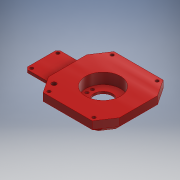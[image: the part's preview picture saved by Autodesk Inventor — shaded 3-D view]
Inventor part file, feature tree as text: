
AUTODESK INVENTOR PART (.ipt)
format: ipt  version: 2018 (Build 220112000, 112)  size: 877,568 bytes
history: native  units: mm
features: sketch x21, extrude x20, mirror x5, projected_geometry x4, chamfer x2, other x2, pattern_circular x2, fillet x1
ambient origin geometry x8: Origin, YZ Plane, XZ Plane, XY Plane, X Axis, Y Axis, Z Axis, Center Point
bodies: Body1 (feature_tree)
feature tree (57):
  extrude  "押し出し2"  Depth=12.0mm TaperAngle=0.0deg
  extrude  "押し出し3"  Depth=17.0mm
  extrude  "押し出し4"  Depth=10.0mm TaperAngle=0.0deg
  extrude  "押し出し5"  Depth=36.5mm
  extrude  "押し出し6"  Depth=6.0mm TaperAngle=0.0deg
  chamfer  "面取り1"  Distance=25.0mm
  extrude  "押し出し7"  Depth=3.0mm
  extrude  "押し出し8"  Depth=3.0mm
  mirror  "ミラー1"
  other  "作業平面1"
  extrude  "押し出し9"  Depth=2.5mm
  extrude  "押し出し10"  Depth=5.0mm TaperAngle=0.0deg
  pattern_circular  "円形状パターン1"  [2 undecoded]
  sketch  "スケッチ12"
  extrude  "押し出し12"  Depth=2.0mm
  pattern_circular  "円形状パターン2"  [2 undecoded]
  extrude  "押し出し11"  Depth=2.0mm
  extrude  "押し出し13"  Depth=4.0mm TaperAngle=0.0deg
  extrude  "押し出し14"  Depth=2.0mm TaperAngle=45.0deg
  mirror  "ミラー3"
  extrude  "押し出し15"  Depth=2.0mm
  extrude  "押し出し16"  Depth=5.0mm
  fillet  "フィレット1"  Radius=7.0mm
  mirror  "ミラー4"
  chamfer  "面取り3"  Angle=45.0deg  [1 undecoded]
  extrude  "押し出し17"  Depth=3.0mm
  mirror  "ミラー5"
  mirror  "ミラー6"
  other  "エンボス1"
  extrude  "押し出し20"  Depth=3.0mm
  extrude  "押し出し19"  Depth=60.0mm
  extrude  "押し出し21"  Depth=10.0mm TaperAngle=0.0deg
  extrude  "押し出し22"  Depth=29.0mm
  sketch  "スケッチ2"
  sketch  "スケッチ3"
  sketch  "スケッチ4"
  sketch  "スケッチ5"
  sketch  "スケッチ6"
  sketch  "スケッチ7"
  projected_geometry  "投影ループ1"
  sketch  "スケッチ8"
  sketch  "スケッチ9"
  sketch  "スケッチ10"
  projected_geometry  "投影ループ2"
  sketch  "スケッチ11"
  sketch  "スケッチ13"
  sketch  "スケッチ14"
  sketch  "スケッチ15"
  sketch  "スケッチ16"
  sketch  "スケッチ17"
  sketch  "スケッチ18"
  sketch  "スケッチ21"
  projected_geometry  "投影ループ3"
  sketch  "スケッチ22"
  projected_geometry  "投影ループ4"
  sketch  "スケッチ23"
  sketch  "スケッチ24"
note: 5 required parameter values undecoded (feature->parameter linkage not recoverable at this tier; creation-order binding heuristic only, values carry confidence <= 0.55)
